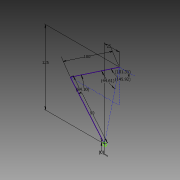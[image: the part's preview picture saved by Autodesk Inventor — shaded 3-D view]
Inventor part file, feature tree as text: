
AUTODESK INVENTOR PART (.ipt)
format: ipt  version: 2020 (Build 240168000, 168)  size: 80,896 bytes
history: native  units: mm
features: sketch x1
ambient origin geometry x8: Origin, YZ Plane, XZ Plane, XY Plane, X Axis, Y Axis, Z Axis, Center Point
feature tree (1):
  sketch  "Sketch1"  dims[d0=90.0mm d1=100.0mm d4=25.46786mm d5=14.678367mm d6=7.785941mm d7=17.681919mm d8=25.0mm d9=125.0mm d10=0.0mm d11=0.0mm]
